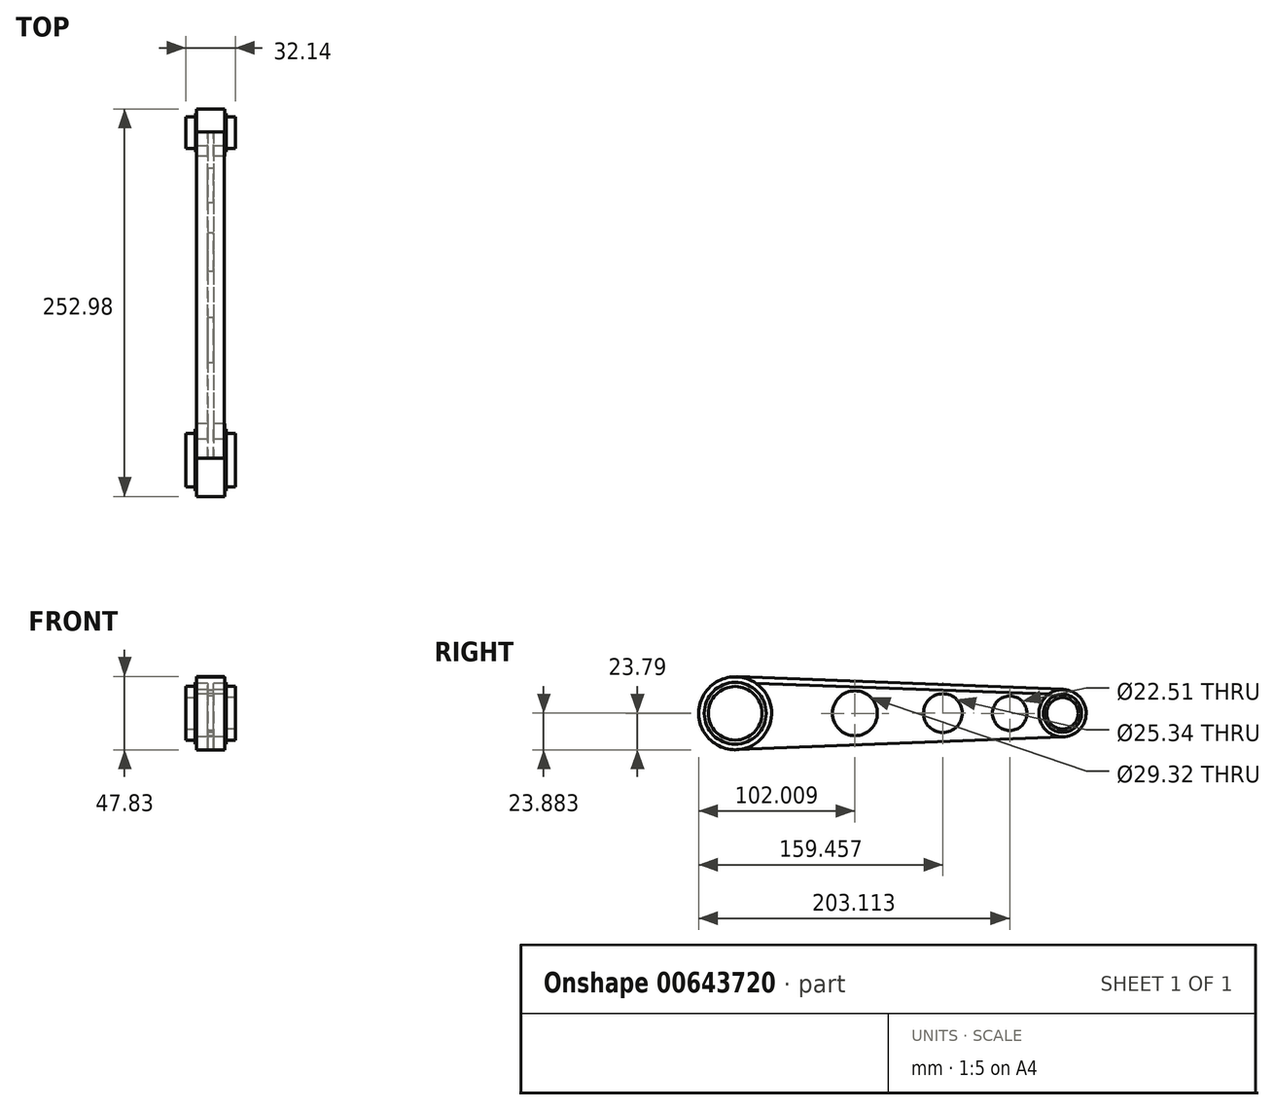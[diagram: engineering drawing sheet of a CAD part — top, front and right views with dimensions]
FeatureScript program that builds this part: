
annotation { "Feature Type Name" : "Feature", "Feature Type Description" : "" }
export const myFeature = defineFeature(function(context is Context, id is Id, definition is map)
    precondition{}
    {
        {
            var Q0;
            Q0=qCreatedBy(makeId("Right.planeOp"),FACE);
            var sketch = newSketch(context, id + "F0", { "sketchPlane" : qUnion([Q0])});
            skCircle(sketch, "E0", {"center": v(-42.23, 0) * mm, "radius": 5.96 * mm});
            skCircle(sketch, "E1", {"center": v(30.58, 0) * mm, "radius": 3.5 * mm});
            skCircle(sketch, "E2", {"center": v(-15.59, 0) * mm, "radius": 5 * mm});
            skCircle(sketch, "E3", {"center": v(3.98, 0.03) * mm, "radius": 4.31 * mm});
            skCircle(sketch, "E4", {"center": v(18.85, 0) * mm, "radius": 3.83 * mm});
            skCircle(sketch, "E5", {"center": v(-42.23, 0) * mm, "radius": 6.88 * mm});
            skCircle(sketch, "E6", {"center": v(30.58, 0) * mm, "radius": 4.23 * mm});
            skCircle(sketch, "E7", {"center": v(30.58, 0) * mm, "radius": 5.25 * mm});
            skCircle(sketch, "E8", {"center": v(-42.23, 0) * mm, "radius": 8.1 * mm});
            skLineSegment(sketch, "E9", {"start": v(-41.58, 8.08) * mm, "end": v(30.78, 5.25) * mm});
            skLineSegment(sketch, "E10", {"start": v(30.68, -5.25) * mm, "end": v(-41.9, -8.1) * mm});
            skSolve(sketch);
        }
        {
            var Q0;
            Q0=makeQuery(id+"F0.imprint","IMPRINT",FACE,{"disambiguationData":[TD([[makeQuery(id+"F0.imprint","IMPRINT",EDGE,{"derivedFrom":sQuery(id+"F0.wireOp",EDGE,"E2")}),-1.0]])]});
            extrude(context, id + "F1", {"entities" : qUnion([Q0]), "depth" : 1.27 * mm, "offsetDistance" : 25.4 * mm});
        }
        {
            var Q0;
            Q0=makeQuery(id+"F0.imprint","IMPRINT",FACE,{"disambiguationData":[TD([[makeQuery(id+"F0.imprint","IMPRINT",EDGE,{"derivedFrom":sQuery(id+"F0.wireOp",EDGE,"E5")}),-1.0]])]});
            var Q1;
            Q1=makeQuery(id+"F0.imprint","IMPRINT",FACE,{"disambiguationData":[TD([[makeQuery(id+"F0.imprint","IMPRINT",EDGE,{"derivedFrom":sQuery(id+"F0.wireOp",EDGE,"E6")}),-1.0]])]});
            extrude(context, id + "F2", {"entities" : qUnion([Q0, Q1]), "operationType" : NewBodyOperationType.ADD, "depth" : 3.8 * mm, "offsetDistance" : 25.4 * mm});
        }
        {
            var Q0;
            Q0=makeQuery(id+"F0.imprint","IMPRINT",FACE,{"disambiguationData":[TD([[makeQuery(id+"F0.imprint","IMPRINT",EDGE,{"derivedFrom":sQuery(id+"F0.wireOp",EDGE,"E5")}),-1.0]])]});
            var Q1;
            Q1=makeQuery(id+"F0.imprint","IMPRINT",FACE,{"disambiguationData":[TD([[makeQuery(id+"F0.imprint","IMPRINT",EDGE,{"derivedFrom":sQuery(id+"F0.wireOp",EDGE,"E6")}),-1.0]])]});
            extrude(context, id + "F3", {"entities" : qUnion([Q0, Q1]), "operationType" : NewBodyOperationType.ADD, "oppositeDirection" : true, "depth" : 2.54 * mm, "offsetDistance" : 25.4 * mm});
        }
        {
            var Q0;
            Q0=qCreatedBy(makeId("Right.planeOp"),FACE);
            var sketch = newSketch(context, id + "F4", { "sketchPlane" : qUnion([Q0])});
            skLineSegment(sketch, "E11", {"start": v(30.79, 5.4) * mm, "end": v(-41.79, 8.19) * mm});
            skLineSegment(sketch, "E12", {"start": v(-41.79, 8.19) * mm, "end": v(-41.79, 6.8) * mm});
            skLineSegment(sketch, "E13", {"start": v(-41.79, 6.8) * mm, "end": v(30.7, 4.2) * mm});
            skLineSegment(sketch, "E14", {"start": v(30.7, 4.2) * mm, "end": v(30.79, 5.4) * mm});
            skSolve(sketch);
        }
        {
            var Q0;
            Q0 = qSketchRegion(id + "F4", true);
            extrude(context, id + "F5", {"entities" : qUnion([Q0]), "operationType" : NewBodyOperationType.ADD, "oppositeDirection" : true, "depth" : 2.54 * mm, "offsetDistance" : 25.4 * mm});
        }
        {
            var Q0;
            Q0 = qSketchRegion(id + "F4", true);
            var Q1;
            Q1=makeQuery(id+"F4.imprint","IMPRINT",FACE,{"disambiguationData":[TD([[makeQuery(id+"F4.imprint","IMPRINT",EDGE,{"derivedFrom":sQuery(id+"F4.wireOp",EDGE,"E11")}),1.0]])]});
            extrude(context, id + "F6", {"entities" : qUnion([Q0, Q1]), "operationType" : NewBodyOperationType.ADD, "oppositeDirection" : true, "depth" : 2.5 * mm, "offsetDistance" : 25.4 * mm});
        }
        {
            var Q0;
            Q0=makeQuery(id+"F0.imprint","IMPRINT",FACE,{"disambiguationData":[TD([[makeQuery(id+"F0.imprint","IMPRINT",EDGE,{"derivedFrom":sQuery(id+"F0.wireOp",EDGE,"E0")}),-1.0]])]});
            var Q1;
            Q1=makeQuery(id+"F0.imprint","IMPRINT",FACE,{"disambiguationData":[TD([[makeQuery(id+"F0.imprint","IMPRINT",EDGE,{"derivedFrom":sQuery(id+"F0.wireOp",EDGE,"E1")}),-1.0]])]});
            extrude(context, id + "F7", {"entities" : qUnion([Q0, Q1]), "operationType" : NewBodyOperationType.ADD, "depth" : 1.78 * mm, "offsetDistance" : 25.4 * mm});
        }
        {
            var Q0;
            Q0=makeQuery(id+"F4.imprint","IMPRINT",FACE,{"disambiguationData":[TD([[makeQuery(id+"F4.imprint","IMPRINT",EDGE,{"derivedFrom":sQuery(id+"F4.wireOp",EDGE,"E11")}),1.0]])]});
            extrude(context, id + "F8", {"entities" : qUnion([Q0]), "operationType" : NewBodyOperationType.ADD, "depth" : 3.66 * mm, "offsetDistance" : 25.4 * mm});
        }
        {
            var Q0;
            Q0=makeQuery(id+"F0.imprint","IMPRINT",FACE,{"disambiguationData":[TD([[makeQuery(id+"F0.imprint","IMPRINT",EDGE,{"derivedFrom":sQuery(id+"F0.wireOp",EDGE,"E1")}),-1.0]])]});
            var Q1;
            Q1=makeQuery(id+"F0.imprint","IMPRINT",FACE,{"disambiguationData":[TD([[makeQuery(id+"F0.imprint","IMPRINT",EDGE,{"derivedFrom":sQuery(id+"F0.wireOp",EDGE,"E0")}),-1.0]])]});
            extrude(context, id + "F9", {"entities" : qUnion([Q0, Q1]), "operationType" : NewBodyOperationType.ADD, "depth" : 4.06 * mm, "offsetDistance" : 25.4 * mm});
        }
        {
            var Q0;
            Q0=makeQuery(id+"F0.imprint","IMPRINT",FACE,{"disambiguationData":[TD([[makeQuery(id+"F0.imprint","IMPRINT",EDGE,{"derivedFrom":sQuery(id+"F0.wireOp",EDGE,"E0")}),-1.0]])]});
            extrude(context, id + "F10", {"entities" : qUnion([Q0]), "operationType" : NewBodyOperationType.ADD, "oppositeDirection" : true, "depth" : 2.8 * mm, "offsetDistance" : 25.4 * mm});
        }
        {
            var Q0;
            Q0=makeQuery(id+"F0.imprint","IMPRINT",FACE,{"disambiguationData":[TD([[makeQuery(id+"F0.imprint","IMPRINT",EDGE,{"derivedFrom":sQuery(id+"F0.wireOp",EDGE,"E1")}),-1.0]])]});
            extrude(context, id + "F11", {"entities" : qUnion([Q0]), "operationType" : NewBodyOperationType.ADD, "oppositeDirection" : true, "depth" : 2.77 * mm, "offsetDistance" : 25.4 * mm});
        }
        {
            var Q0;
            Q0=makeQuery(id+"F0.imprint","IMPRINT",FACE,{"disambiguationData":[TD([[makeQuery(id+"F0.imprint","IMPRINT",EDGE,{"derivedFrom":sQuery(id+"F0.wireOp",EDGE,"E0")}),1.0]])]});
            var Q1;
            Q1=makeQuery(id+"F0.imprint","IMPRINT",FACE,{"disambiguationData":[TD([[makeQuery(id+"F0.imprint","IMPRINT",EDGE,{"derivedFrom":sQuery(id+"F0.wireOp",EDGE,"E1")}),1.0]])]});
            extrude(context, id + "F12", {"entities" : qUnion([Q0, Q1]), "operationType" : NewBodyOperationType.ADD, "depth" : 6.1 * mm, "offsetDistance" : 25.4 * mm});
        }
        {
            var Q0;
            Q0=makeQuery(id+"F0.imprint","IMPRINT",FACE,{"disambiguationData":[TD([[makeQuery(id+"F0.imprint","IMPRINT",EDGE,{"derivedFrom":sQuery(id+"F0.wireOp",EDGE,"E1")}),1.0]])]});
            var Q1;
            Q1=makeQuery(id+"F0.imprint","IMPRINT",FACE,{"disambiguationData":[TD([[makeQuery(id+"F0.imprint","IMPRINT",EDGE,{"derivedFrom":sQuery(id+"F0.wireOp",EDGE,"E0")}),1.0]])]});
            extrude(context, id + "F13", {"entities" : qUnion([Q0, Q1]), "operationType" : NewBodyOperationType.ADD, "oppositeDirection" : true, "depth" : 4.85 * mm, "offsetDistance" : 25.4 * mm});
        }
        {
            var Q0;
            Q0=makeQuery(id+"F1.opExtrude","SWEPT_BODY",BODY,{"disambiguationData":[OSD([sQuery(id+"F0.wireOp",EDGE,"E2"),sQuery(id+"F0.wireOp",EDGE,"E3"),sQuery(id+"F0.wireOp",EDGE,"E4"),sQuery(id+"F0.wireOp",EDGE,"E7"),sQuery(id+"F0.wireOp",EDGE,"E8"),sQuery(id+"F0.wireOp",EDGE,"E9"),sQuery(id+"F0.wireOp",EDGE,"E10")])]});
            var Q1;
            Q1=qCreatedBy(makeId("Origin.pointOp"),VERTEX);
            transform(context, id + "F14", {"entities" : qUnion([Q0]), "transformType" : TransformType.SCALE_UNIFORMLY, "scale" : 1.45, "scalePoint" : qUnion([Q1]), "makeCopy" : false});
        }
        {
            var Q0;
            Q0=makeQuery(id+"F1.opExtrude","SWEPT_BODY",BODY,{"disambiguationData":[OSD([sQuery(id+"F0.wireOp",EDGE,"E2"),sQuery(id+"F0.wireOp",EDGE,"E3"),sQuery(id+"F0.wireOp",EDGE,"E4"),sQuery(id+"F0.wireOp",EDGE,"E7"),sQuery(id+"F0.wireOp",EDGE,"E8"),sQuery(id+"F0.wireOp",EDGE,"E9"),sQuery(id+"F0.wireOp",EDGE,"E10")])]});
            transform(context, id + "F15", {"entities" : qUnion([Q0]), "transformType" : TransformType.TRANSLATION_3D, "dx" : 0 * mm, "dy" : -15.75 * mm, "dz" : 0 * mm, "makeCopy" : false});
        }
        {
            var Q0;
            Q0=makeQuery(id+"F1.opExtrude","SWEPT_BODY",BODY,{"disambiguationData":[OSD([sQuery(id+"F0.wireOp",EDGE,"E2"),sQuery(id+"F0.wireOp",EDGE,"E3"),sQuery(id+"F0.wireOp",EDGE,"E4"),sQuery(id+"F0.wireOp",EDGE,"E7"),sQuery(id+"F0.wireOp",EDGE,"E8"),sQuery(id+"F0.wireOp",EDGE,"E9"),sQuery(id+"F0.wireOp",EDGE,"E10")])]});
            var Q1;
            Q1=sQuery(id+"F0.wireOp",EDGE,"E3");
            transform(context, id + "F16", {"entities" : qUnion([Q0]), "transformType" : TransformType.TRANSLATION_3D, "dx" : 16.26 * mm, "dy" : 0 * mm, "dz" : 0 * mm, "makeCopy" : false});
        }
        {
            var Q0;
            Q0=makeQuery(id+"F1.opExtrude","SWEPT_BODY",BODY,{"disambiguationData":[OSD([sQuery(id+"F0.wireOp",EDGE,"E2"),sQuery(id+"F0.wireOp",EDGE,"E3"),sQuery(id+"F0.wireOp",EDGE,"E4"),sQuery(id+"F0.wireOp",EDGE,"E7"),sQuery(id+"F0.wireOp",EDGE,"E8"),sQuery(id+"F0.wireOp",EDGE,"E9"),sQuery(id+"F0.wireOp",EDGE,"E10")])]});
            var Q1;
            Q1=sQuery(id+"F0.wireOp",EDGE,"E10");
            var Q2;
            Q2=sQuery(id+"F0.wireOp",EDGE,"E3");
            var Q3;
            Q3=qCreatedBy(makeId("Origin.pointOp"),VERTEX);
            transform(context, id + "F17", {"entities" : qUnion([Q0]), "transformType" : TransformType.SCALE_UNIFORMLY, "scale" : 1.35, "scalePoint" : qUnion([Q3]), "makeCopy" : false});
        }
        {
            var Q0;
            Q0=makeQuery(id+"F1.opExtrude","SWEPT_BODY",BODY,{"disambiguationData":[OSD([sQuery(id+"F0.wireOp",EDGE,"E2"),sQuery(id+"F0.wireOp",EDGE,"E3"),sQuery(id+"F0.wireOp",EDGE,"E4"),sQuery(id+"F0.wireOp",EDGE,"E7"),sQuery(id+"F0.wireOp",EDGE,"E8"),sQuery(id+"F0.wireOp",EDGE,"E9"),sQuery(id+"F0.wireOp",EDGE,"E10")])]});
            var Q1;
            Q1=sQuery(id+"F0.wireOp",EDGE,"E3");
            transform(context, id + "F18", {"entities" : qUnion([Q0]), "transformType" : TransformType.TRANSLATION_3D, "dx" : -6.1 * mm, "dy" : -10.92 * mm, "dz" : 0 * mm, "makeCopy" : false});
        }
        {
            var Q0;
            Q0=makeQuery(id+"F1.opExtrude","SWEPT_BODY",BODY,{"disambiguationData":[OSD([sQuery(id+"F0.wireOp",EDGE,"E2"),sQuery(id+"F0.wireOp",EDGE,"E3"),sQuery(id+"F0.wireOp",EDGE,"E4"),sQuery(id+"F0.wireOp",EDGE,"E7"),sQuery(id+"F0.wireOp",EDGE,"E8"),sQuery(id+"F0.wireOp",EDGE,"E9"),sQuery(id+"F0.wireOp",EDGE,"E10")])]});
            var Q1;
            Q1=qCreatedBy(makeId("Origin.pointOp"),VERTEX);
            transform(context, id + "F19", {"entities" : qUnion([Q0]), "transformType" : TransformType.SCALE_UNIFORMLY, "scale" : 1.5, "scalePoint" : qUnion([Q1]), "makeCopy" : false});
        }
    });
